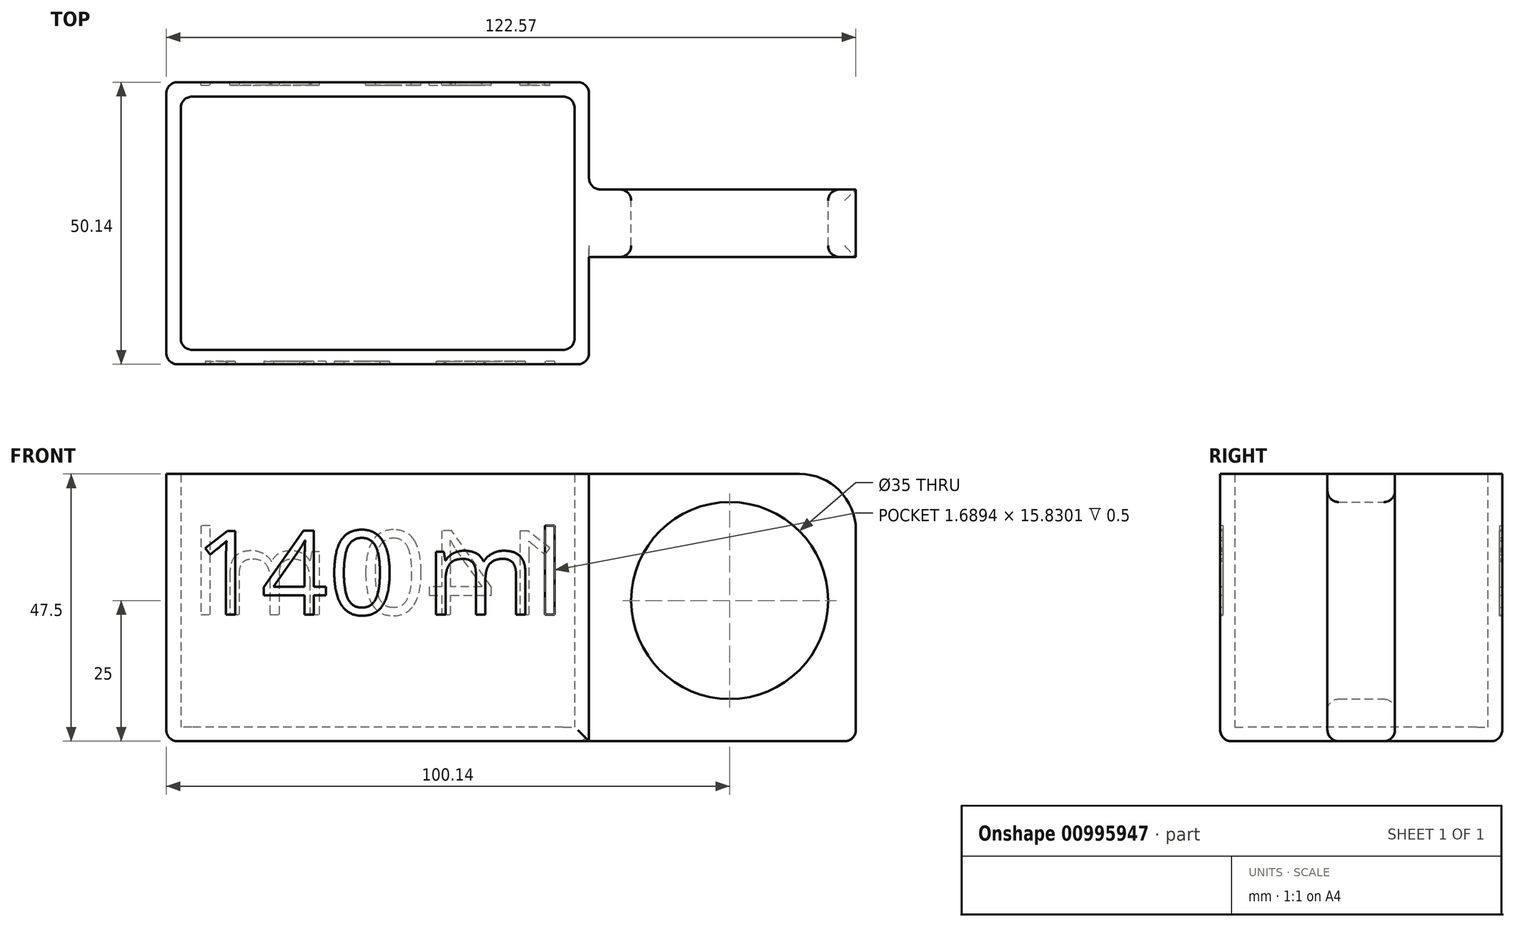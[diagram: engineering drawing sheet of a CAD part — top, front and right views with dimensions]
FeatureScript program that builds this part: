
annotation { "Feature Type Name" : "Feature", "Feature Type Description" : "" }
export const myFeature = defineFeature(function(context is Context, id is Id, definition is map)
    precondition{}
    {
        {
            var Q0;
            Q0=qCreatedBy(makeId("Top.planeOp"),FACE);
            var sketch = newSketch(context, id + "F0", { "sketchPlane" : qUnion([Q0])});
            skLineSegment(sketch, "E0.bottom", {"start": v(35, 22.5) * mm, "end": v(-35, 22.5) * mm});
            skLineSegment(sketch, "E0.top", {"start": v(35, -22.5) * mm, "end": v(-35, -22.5) * mm});
            skLineSegment(sketch, "E0.left", {"start": v(35, 22.5) * mm, "end": v(35, -22.5) * mm});
            skLineSegment(sketch, "E0.right", {"start": v(-35, 22.5) * mm, "end": v(-35, -22.5) * mm});
            skPoint(sketch, "E0.middle", {"position": v(0, 0) * mm});
            skLineSegment(sketch, "E1.0", {"start": v(-37.57, 25.07) * mm, "end": v(-37.57, -25.07) * mm});
            skLineSegment(sketch, "E1.1", {"start": v(37.57, 25.07) * mm, "end": v(-37.57, 25.07) * mm});
            skLineSegment(sketch, "E1.2", {"start": v(37.57, 25.07) * mm, "end": v(37.57, -25.07) * mm});
            skLineSegment(sketch, "E1.3", {"start": v(37.57, -25.07) * mm, "end": v(-37.57, -25.07) * mm});
            skSolve(sketch);
        }
        {
            var Q0;
            Q0 = qSketchRegion(id + "F0", true);
            extrude(context, id + "F1", {"entities" : qUnion([Q0]), "depth" : 45 * mm, "offsetDistance" : 25 * mm});
        }
        {
            var Q0;
            Q0=makeQuery(id+"F0.imprint","IMPRINT",FACE,{"disambiguationData":[TD([[makeQuery(id+"F0.imprint","IMPRINT",EDGE,{"derivedFrom":sQuery(id+"F0.wireOp",EDGE,"E0.bottom")}),1.0]])]});
            var Q1;
            Q1=makeQuery(id+"F0.imprint","IMPRINT",FACE,{"disambiguationData":[TD([[makeQuery(id+"F0.imprint","IMPRINT",EDGE,{"derivedFrom":sQuery(id+"F0.wireOp",EDGE,"E0.bottom")}),-1.0]])]});
            extrude(context, id + "F2", {"entities" : qUnion([Q0, Q1]), "operationType" : NewBodyOperationType.ADD, "oppositeDirection" : true, "depth" : 2.5 * mm, "offsetDistance" : 25 * mm});
        }
        {
            var Q0;
            Q0=makeQuery(id+"F1.opExtrude","SWEPT_EDGE",EDGE,{"disambiguationData":[OSD([sQuery(id+"F0.wireOp",EDGE,"E0.bottom"),sQuery(id+"F0.wireOp",EDGE,"E0.right")])]});
            var Q1;
            Q1=makeQuery(id+"F1.opExtrude","CAP_EDGE",EDGE,{"disambiguationData":[OSD([sQuery(id+"F0.wireOp",EDGE,"E0.right")])],"isStart":true});
            var Q2;
            Q2=makeQuery(id+"F1.opExtrude","CAP_EDGE",EDGE,{"disambiguationData":[OSD([sQuery(id+"F0.wireOp",EDGE,"E0.bottom")])],"isStart":true});
            var Q3;
            Q3=makeQuery(id+"F1.opExtrude","SWEPT_EDGE",EDGE,{"disambiguationData":[OSD([sQuery(id+"F0.wireOp",EDGE,"E0.top"),sQuery(id+"F0.wireOp",EDGE,"E0.right")])]});
            var Q4;
            Q4=makeQuery(id+"F1.opExtrude","SWEPT_EDGE",EDGE,{"disambiguationData":[OSD([sQuery(id+"F0.wireOp",EDGE,"E0.bottom"),sQuery(id+"F0.wireOp",EDGE,"E0.left")])]});
            var Q5;
            Q5=makeQuery(id+"F1.opExtrude","CAP_EDGE",EDGE,{"disambiguationData":[OSD([sQuery(id+"F0.wireOp",EDGE,"E0.left")])],"isStart":true});
            var Q6;
            Q6=makeQuery(id+"F1.opExtrude","CAP_EDGE",EDGE,{"disambiguationData":[OSD([sQuery(id+"F0.wireOp",EDGE,"E0.top")])],"isStart":true});
            var Q7;
            Q7=makeQuery(id+"F1.opExtrude","SWEPT_EDGE",EDGE,{"disambiguationData":[OSD([sQuery(id+"F0.wireOp",EDGE,"E0.top"),sQuery(id+"F0.wireOp",EDGE,"E0.left")])]});
            var Q8;
            {var subQ0=sQuery(id+"F0.wireOp",EDGE,"E1.3");var subQ1=sQuery(id+"F0.wireOp",EDGE,"E1.2");Q8=makeQuery(id+"F2.boolean.opBoolean","MERGE",EDGE,{"derivedFrom":[makeQuery(id+"F1.opExtrude","SWEPT_EDGE",EDGE,{"disambiguationData":[OSD([subQ1,subQ0])]}),makeQuery(id+"F2.opExtrude","SWEPT_EDGE",EDGE,{"disambiguationData":[OSD([subQ1,subQ0])]})]});}
            var Q9;
            {var subQ0=sQuery(id+"F0.wireOp",EDGE,"E1.2");var subQ1=sQuery(id+"F0.wireOp",EDGE,"E1.1");Q9=makeQuery(id+"F2.boolean.opBoolean","MERGE",EDGE,{"derivedFrom":[makeQuery(id+"F1.opExtrude","SWEPT_EDGE",EDGE,{"disambiguationData":[OSD([subQ1,subQ0])]}),makeQuery(id+"F2.opExtrude","SWEPT_EDGE",EDGE,{"disambiguationData":[OSD([subQ1,subQ0])]})]});}
            var Q10;
            {var subQ0=sQuery(id+"F0.wireOp",EDGE,"E1.3");var subQ1=sQuery(id+"F0.wireOp",EDGE,"E1.0");Q10=makeQuery(id+"F2.boolean.opBoolean","MERGE",EDGE,{"derivedFrom":[makeQuery(id+"F1.opExtrude","SWEPT_EDGE",EDGE,{"disambiguationData":[OSD([subQ1,subQ0])]}),makeQuery(id+"F2.opExtrude","SWEPT_EDGE",EDGE,{"disambiguationData":[OSD([subQ1,subQ0])]})]});}
            var Q11;
            {var subQ0=sQuery(id+"F0.wireOp",EDGE,"E1.1");var subQ1=sQuery(id+"F0.wireOp",EDGE,"E1.0");Q11=makeQuery(id+"F2.boolean.opBoolean","MERGE",EDGE,{"derivedFrom":[makeQuery(id+"F1.opExtrude","SWEPT_EDGE",EDGE,{"disambiguationData":[OSD([subQ1,subQ0])]}),makeQuery(id+"F2.opExtrude","SWEPT_EDGE",EDGE,{"disambiguationData":[OSD([subQ1,subQ0])]})]});}
            var Q12;
            Q12=makeQuery(id+"F2.opExtrude","CAP_EDGE",EDGE,{"disambiguationData":[OSD([sQuery(id+"F0.wireOp",EDGE,"E1.3")])],"isStart":false});
            var Q13;
            Q13=makeQuery(id+"F2.opExtrude","CAP_EDGE",EDGE,{"disambiguationData":[OSD([sQuery(id+"F0.wireOp",EDGE,"E1.0")])],"isStart":false});
            var Q14;
            Q14=makeQuery(id+"F2.opExtrude","CAP_EDGE",EDGE,{"disambiguationData":[OSD([sQuery(id+"F0.wireOp",EDGE,"E1.1")])],"isStart":false});
            fillet(context, id + "F3", {"entities" : qUnion([Q0, Q1, Q2, Q3, Q4, Q5, Q6, Q7, Q8, Q9, Q10, Q11, Q12, Q13, Q14]), "radius" : 2 * mm, "tangentPropagation" : true, "allowEdgeOverflow" : false});
        }
        {
            var Q0;
            Q0=qCreatedBy(makeId("Front.planeOp"),FACE);
            var sketch = newSketch(context, id + "F4", { "sketchPlane" : qUnion([Q0])});
            skLineSegment(sketch, "E2.bottom", {"start": v(37.57, 45) * mm, "end": v(75, 45) * mm});
            skLineSegment(sketch, "E2.top", {"start": v(37.57, -2.5) * mm, "end": v(85, -2.5) * mm});
            skLineSegment(sketch, "E2.left", {"start": v(37.57, 45) * mm, "end": v(37.57, -2.5) * mm});
            skLineSegment(sketch, "E2.right", {"start": v(85, 35) * mm, "end": v(85, -2.5) * mm});
            skCircle(sketch, "E3", {"center": v(62.57, 22.5) * mm, "radius": 17.5 * mm});
            skPoint(sketch, "E4.visualSharp", {"position": v(85, 45) * mm});
            skArc(sketch, "E4.filletArc", {"start": v(85, 35) * mm, "mid": v(82.07, 42.07) * mm, "end": v(75, 45) * mm});
            skSolve(sketch);
        }
        {
            var Q0;
            Q0=makeQuery(id+"F4.imprint","IMPRINT",FACE,{"disambiguationData":[TD([[makeQuery(id+"F4.imprint","IMPRINT",EDGE,{"derivedFrom":sQuery(id+"F4.wireOp",EDGE,"E2.bottom")}),-1.0]])]});
            extrude(context, id + "F5", {"entities" : qUnion([Q0]), "operationType" : NewBodyOperationType.ADD, "endBound" : BoundingType.SYMMETRIC, "depth" : 12 * mm, "offsetDistance" : 25 * mm});
        }
        {
            var Q0;
            Q0=makeQuery(id+"F5.opExtrude","CAP_EDGE",EDGE,{"disambiguationData":[OSD([sQuery(id+"F4.wireOp",EDGE,"E2.left")])],"isStart":false});
            var Q1;
            Q1=makeQuery(id+"F5.opExtrude","CAP_EDGE",EDGE,{"disambiguationData":[OSD([sQuery(id+"F4.wireOp",EDGE,"E2.left")])],"isStart":true});
            var Q2;
            {var subQ0=sQuery(id+"F0.wireOp",EDGE,"E1.1");var subQ1=sQuery(id+"F0.wireOp",EDGE,"E1.2");Q2=makeQuery(id+"F5.boolean.opBoolean","SPLIT",EDGE,{"disambiguationData":[TD([makeQuery(id+"F3.opFillet","BLEND_FACE",FACE,{"disambiguationData":[OSD([subQ0])]})])],"derivedFrom":makeQuery(id+"F2.opExtrude","CAP_EDGE",EDGE,{"disambiguationData":[OSD([subQ1])],"isStart":false})});}
            var Q3;
            Q3=makeQuery(id+"F5.opExtrude","CAP_EDGE",EDGE,{"disambiguationData":[OSD([sQuery(id+"F4.wireOp",EDGE,"E2.top")])],"isStart":true});
            var Q4;
            Q4=makeQuery(id+"F5.opExtrude","CAP_EDGE",EDGE,{"disambiguationData":[OSD([sQuery(id+"F4.wireOp",EDGE,"E2.top")])],"isStart":false});
            var Q5;
            Q5=makeQuery(id+"F5.opExtrude","SWEPT_EDGE",EDGE,{"disambiguationData":[OSD([sQuery(id+"F4.wireOp",EDGE,"E2.top"),sQuery(id+"F4.wireOp",EDGE,"E2.right")])]});
            var Q6;
            Q6=makeQuery(id+"F5.opExtrude","CAP_EDGE",EDGE,{"disambiguationData":[OSD([sQuery(id+"F4.wireOp",EDGE,"E3")])],"isStart":false});
            var Q7;
            Q7=makeQuery(id+"F5.opExtrude","CAP_EDGE",EDGE,{"disambiguationData":[OSD([sQuery(id+"F4.wireOp",EDGE,"E3")])],"isStart":true});
            fillet(context, id + "F6", {"entities" : qUnion([Q0, Q1, Q2, Q3, Q4, Q5, Q6, Q7]), "radius" : 2 * mm, "tangentPropagation" : true, "allowEdgeOverflow" : false});
        }
        {
            var Q0;
            {var subQ0=sQuery(id+"F0.wireOp",EDGE,"E1.3");Q0=makeQuery(id+"F2.boolean.opBoolean","MERGE",FACE,{"derivedFrom":[makeQuery(id+"F1.opExtrude","SWEPT_FACE",FACE,{"disambiguationData":[OSD([subQ0])]}),makeQuery(id+"F2.opExtrude","SWEPT_FACE",FACE,{"disambiguationData":[OSD([subQ0])]})]});}
            var sketch = newSketch(context, id + "F7", { "sketchPlane" : qUnion([Q0])});
            skText(sketch, "E5", { "text": "140 ml", "fontName": "OpenSans-Regular.ttf"});
            const initialGuessF7  = {"E5": [-0.03257, 0.02, 1, 0, 0.015]};
            skSetInitialGuess(sketch, initialGuessF7);
            skSolve(sketch);
        }
        {
            var Q0;
            Q0 = qSketchRegion(id + "F7", true);
            extrude(context, id + "F8", {"entities" : qUnion([Q0]), "operationType" : NewBodyOperationType.REMOVE, "oppositeDirection" : true, "depth" : 0.5 * mm, "offsetDistance" : 25 * mm});
        }
        {
            var Q0;
            Q0 = qSketchRegion(id + "F7", true);
            extrude(context, id + "F9", {"entities" : qUnion([Q0]), "operationType" : NewBodyOperationType.REMOVE, "oppositeDirection" : true, "depth" : 0.5 * mm, "offsetDistance" : 25 * mm});
        }
        {
            var Q0;
            {var subQ0=sQuery(id+"F0.wireOp",EDGE,"E1.1");Q0=makeQuery(id+"F2.boolean.opBoolean","MERGE",FACE,{"derivedFrom":[makeQuery(id+"F1.opExtrude","SWEPT_FACE",FACE,{"disambiguationData":[OSD([subQ0])]}),makeQuery(id+"F2.opExtrude","SWEPT_FACE",FACE,{"disambiguationData":[OSD([subQ0])]})]});}
            var sketch = newSketch(context, id + "F10", { "sketchPlane" : qUnion([Q0])});
            skText(sketch, "E6", { "text": "140 ml", "fontName": "OpenSans-Regular.ttf"});
            const initialGuessF10  = {"E6": [-0.03257, 0.02, 1, 0, 0.015]};
            skSetInitialGuess(sketch, initialGuessF10);
            skSolve(sketch);
        }
        {
            var Q0;
            Q0 = qSketchRegion(id + "F10", true);
            extrude(context, id + "F11", {"entities" : qUnion([Q0]), "operationType" : NewBodyOperationType.REMOVE, "oppositeDirection" : true, "depth" : 0.5 * mm, "offsetDistance" : 25 * mm});
        }
    });
